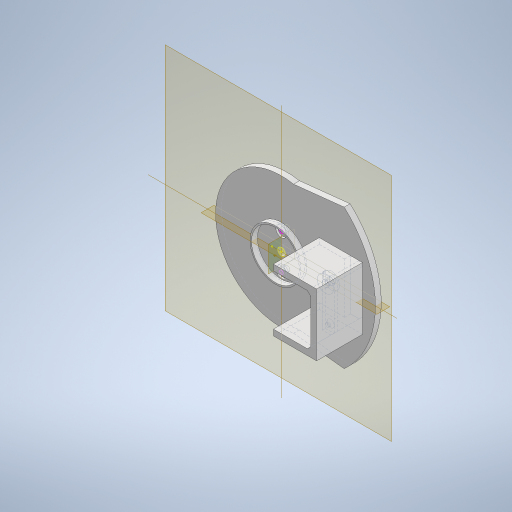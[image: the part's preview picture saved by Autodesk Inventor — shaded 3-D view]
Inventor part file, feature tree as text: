
AUTODESK INVENTOR PART (.ipt)
format: ipt  version: 2023.2 (Build 272271030, 271C)  size: 363,520 bytes
history: native  units: in
note: dims shown in document units (in); Inventor stores cm internally (conversion verified against a paired STEP export)
features: reference x18, other x15, sketch x11, extrude x7, plane x4, hole x2
ambient origin geometry x8: Origin, YZ Plane, XZ Plane, XY Plane, X Axis, Y Axis, Z Axis, Center Point
bodies: Solid1 (feature_tree)
feature tree (57):
  plane  "Work Plane1"
  extrude  "Primary Shaft Bore"  Depth=0.1969in TaperAngle=0.0deg
  extrude  "Large Gear Seat"  Depth=1.7in
  sketch  "Sketch4"  dims[d5=0.1969in d6=0.0in d17=0.55in]
  plane  "Work Plane2"
  sketch  "Sketch5"  dims[d18=0.1181in d19=0.0in]
  other  "Work Axis2"
  other  "Work Axis3"
  plane  "Work Plane5"
  other  "Work Point1"
  sketch  "Sketch7"  dims[d20=0.177in d21=0.315in d22=0.37in d23=0.0625in d24=90.0deg d25=1.0in d26=0.8108in d27=0.2165in]
  other  "Work Point2"
  extrude  "Second Gear Seat"  Depth=0.1969in
  hole  "Hole1"  [1 undecoded]
  extrude  "Extrusion7"  Depth=0.2362in
  sketch  "Sketch10"  dims[d33=0.1969in d34=0.0394in]
  plane  "Work Plane6"
  extrude  "Extrusion8"  Depth=0.1969in
  extrude  "Extrusion9"  Depth=0.0394in
  extrude  "Extrusion10"  Depth=0.2362in TaperAngle=0.0deg
  hole  "Hole2"  [1 undecoded]
  sketch  "Sketch1"  dims[d0=2.2in d1=0.1969in d2=0.0in]
  reference  "Reference1"
  reference  "Reference2"
  reference  "Reference3"
  reference  "Reference4"
  reference  "Reference5"
  sketch  "Sketch2"  dims[d3=1.6in d4=1.7in]
  reference  "Reference6"
  reference  "Reference8"
  reference  "Reference9"
  reference  "Reference11"
  sketch  "Sketch8"  dims[d28=0.2362in d29=0.0in d30=0.0079in]
  sketch  "Sketch9"  dims[d31=0.0039in d32=0.1969in]
  reference  "Reference12"
  reference  "Reference13"
  reference  "Reference14"
  reference  "Reference15"
  reference  "Reference16"
  reference  "Reference17"
  sketch  "Sketch11"  dims[d35=0.0394in d36=0.2362in d37=0.0in]
  reference  "Reference18"
  sketch  "Sketch12"  dims[d38=0.1in d39=0.0039in]
  sketch  "Sketch13"  dims[d40=0.4in d41=0.0in d42=0.4in d43=0.0in d44=0.134in d45=0.75in d46=0.248in d47=0.141in d48=90.0deg d49=1.0in d50=0.8108in]
  reference  "Reference19"
  reference  "Reference20"
  other  "<userpath>\Dropbox\elec\Mechanical\SkimmerSwabbie\_Design_WholeAssem.iam"
  other  "_Design_WholeAssem.iam"
  other  "_Design_SkimmerLid:1"
  other  "SkimmerLid:1"
  other  "SkimmerLidInsert:1"
  other  "<userpath>\Dropbox\elec\Mechanical\SkimmerSwabbie\_Design_TopOfLid.iam"
  other  "_Design_TopOfLid.iam"
  other  "_GearTrain:1"
  other  "Spur Gears:1"
  other  "Spur Gear1:1"
  other  "17HS08-1004S:1"
note: 2 required parameter values undecoded (feature->parameter linkage not recoverable at this tier; creation-order binding heuristic only, values carry confidence <= 0.55)
